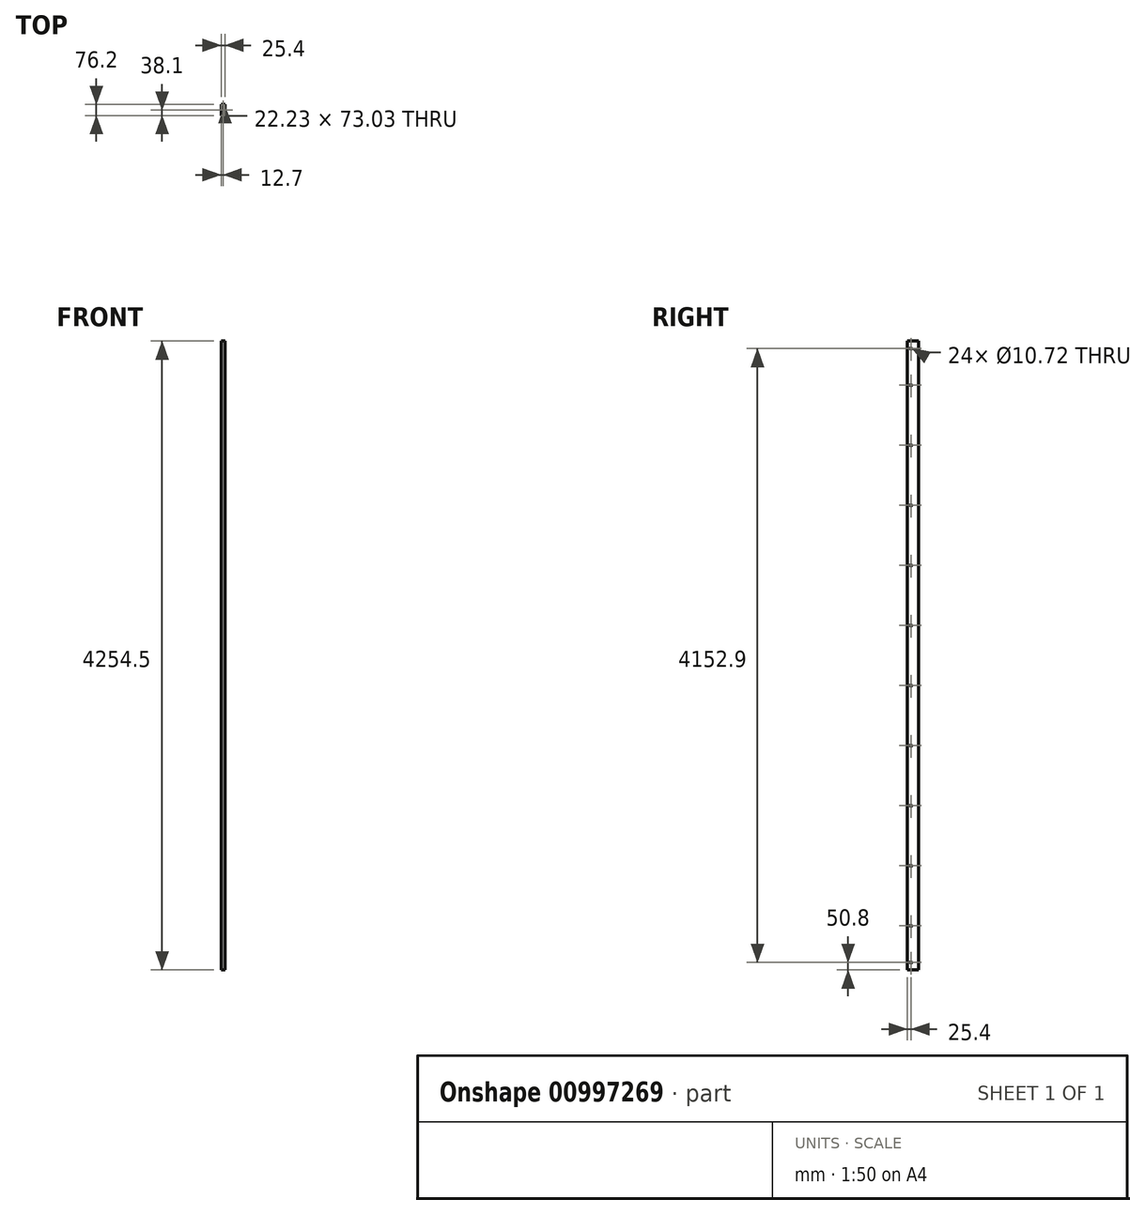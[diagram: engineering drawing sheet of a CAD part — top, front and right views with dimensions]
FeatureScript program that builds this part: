
annotation { "Feature Type Name" : "Feature", "Feature Type Description" : "" }
export const myFeature = defineFeature(function(context is Context, id is Id, definition is map)
    precondition{}
    {
        {
            var Q0;
            Q0=qCreatedBy(makeId("Top.planeOp"),FACE);
            var sketch = newSketch(context, id + "F0", { "sketchPlane" : qUnion([Q0])});
            skLineSegment(sketch, "E0.bottom", {"start": v(-11.11, 36.51) * mm, "end": v(11.11, 36.51) * mm});
            skLineSegment(sketch, "E0.top", {"start": v(-11.11, -36.51) * mm, "end": v(11.11, -36.51) * mm});
            skLineSegment(sketch, "E0.left", {"start": v(-11.11, 36.51) * mm, "end": v(-11.11, -36.51) * mm});
            skLineSegment(sketch, "E0.right", {"start": v(11.11, 36.51) * mm, "end": v(11.11, -36.51) * mm});
            skLineSegment(sketch, "E1.bottom", {"start": v(-12.7, 38.1) * mm, "end": v(12.7, 38.1) * mm});
            skLineSegment(sketch, "E1.top", {"start": v(-12.7, -38.1) * mm, "end": v(12.7, -38.1) * mm});
            skLineSegment(sketch, "E1.left", {"start": v(-12.7, 38.1) * mm, "end": v(-12.7, -38.1) * mm});
            skLineSegment(sketch, "E1.right", {"start": v(12.7, 38.1) * mm, "end": v(12.7, -38.1) * mm});
            skSolve(sketch);
        }
        {
            var Q0;
            Q0 = qSketchRegion(id + "F0", true);
            extrude(context, id + "F1", {"entities" : qUnion([Q0]), "endBound" : BoundingType.SYMMETRIC, "depth" : 4254.5 * mm, "offsetDistance" : 25.4 * mm});
        }
        {
            var Q0;
            Q0=makeQuery(id+"F1.opExtrude","SWEPT_FACE",FACE,{"disambiguationData":[OSD([sQuery(id+"F0.wireOp",EDGE,"E1.right")])]});
            var sketch = newSketch(context, id + "F2", { "sketchPlane" : qUnion([Q0])});
            skPoint(sketch, "E2", {"position": v(-12.7, 203.2) * mm});
            skPoint(sketch, "E3", {"position": v(-12.7, 609.6) * mm});
            skPoint(sketch, "E4", {"position": v(-12.7, 1016) * mm});
            skPoint(sketch, "E5", {"position": v(-12.7, 1422.4) * mm});
            skPoint(sketch, "E6", {"position": v(-12.7, 1828.8) * mm});
            skPoint(sketch, "E7", {"position": v(-12.7, 2076.45) * mm});
            skPoint(sketch, "E8.MirrorP", {"position": v(-12.7, -203.2) * mm});
            skPoint(sketch, "E9.MirrorP", {"position": v(-12.7, -609.6) * mm});
            skPoint(sketch, "E10.MirrorP", {"position": v(-12.7, -1016) * mm});
            skPoint(sketch, "E11.MirrorP", {"position": v(-12.7, -1422.4) * mm});
            skPoint(sketch, "E12.MirrorP", {"position": v(-12.7, -1828.8) * mm});
            skPoint(sketch, "E13.MirrorP", {"position": v(-12.7, -2076.45) * mm});
            skSolve(sketch);
        }
        {
            var Q0;
            Q0=sQuery(id+"F2.wireOp",VERTEX,"E7");
            var Q1;
            Q1=sQuery(id+"F2.wireOp",VERTEX,"E6");
            var Q2;
            Q2=sQuery(id+"F2.wireOp",VERTEX,"E5");
            var Q3;
            Q3=sQuery(id+"F2.wireOp",VERTEX,"E4");
            var Q4;
            Q4=sQuery(id+"F2.wireOp",VERTEX,"E3");
            var Q5;
            Q5=sQuery(id+"F2.wireOp",VERTEX,"E2");
            var Q6;
            Q6=sQuery(id+"F2.wireOp",VERTEX,"E8.MirrorP");
            var Q7;
            Q7=sQuery(id+"F2.wireOp",VERTEX,"E9.MirrorP");
            var Q8;
            Q8=sQuery(id+"F2.wireOp",VERTEX,"E10.MirrorP");
            var Q9;
            Q9=sQuery(id+"F2.wireOp",VERTEX,"E11.MirrorP");
            var Q10;
            Q10=sQuery(id+"F2.wireOp",VERTEX,"E12.MirrorP");
            var Q11;
            Q11=sQuery(id+"F2.wireOp",VERTEX,"E13.MirrorP");
            var Q12;
            Q12=makeQuery(id+"F1.opExtrude","SWEPT_BODY",BODY,{"disambiguationData":[OSD([sQuery(id+"F0.wireOp",EDGE,"E0.bottom"),sQuery(id+"F0.wireOp",EDGE,"E0.top"),sQuery(id+"F0.wireOp",EDGE,"E0.left"),sQuery(id+"F0.wireOp",EDGE,"E0.right"),sQuery(id+"F0.wireOp",EDGE,"E1.bottom"),sQuery(id+"F0.wireOp",EDGE,"E1.top"),sQuery(id+"F0.wireOp",EDGE,"E1.left"),sQuery(id+"F0.wireOp",EDGE,"E1.right")])]});
            hole(context, id + "F3", {"style" : HoleStyle.SIMPLE, "endStyle" : HoleEndStyle.THROUGH, "standardTappedOrClearance" : lookupTablePath({ "fit" : "Loose (ASME)", "standard" : "ANSI", "size" : "3/8", "type" : "Clearance" }), "standardBlindInLast" : lookupTablePath({ "fit" : "Loose", "standard" : "ANSI", "engagement" : "75%", "pitch" : "16 tpi", "size" : "3/8", "type" : "Clearance & tapped" }), "holeDiameter" : 10.72 * mm, "majorDiameter" : 6.35 * mm, "isTappedThrough" : true, "tappedDepth" : 12.7 * mm, "tapClearance" : 3, "locations" : qUnion([Q0, Q1, Q2, Q3, Q4, Q5, Q6, Q7, Q8, Q9, Q10, Q11]), "scope" : qUnion([Q12])});
        }
    });
